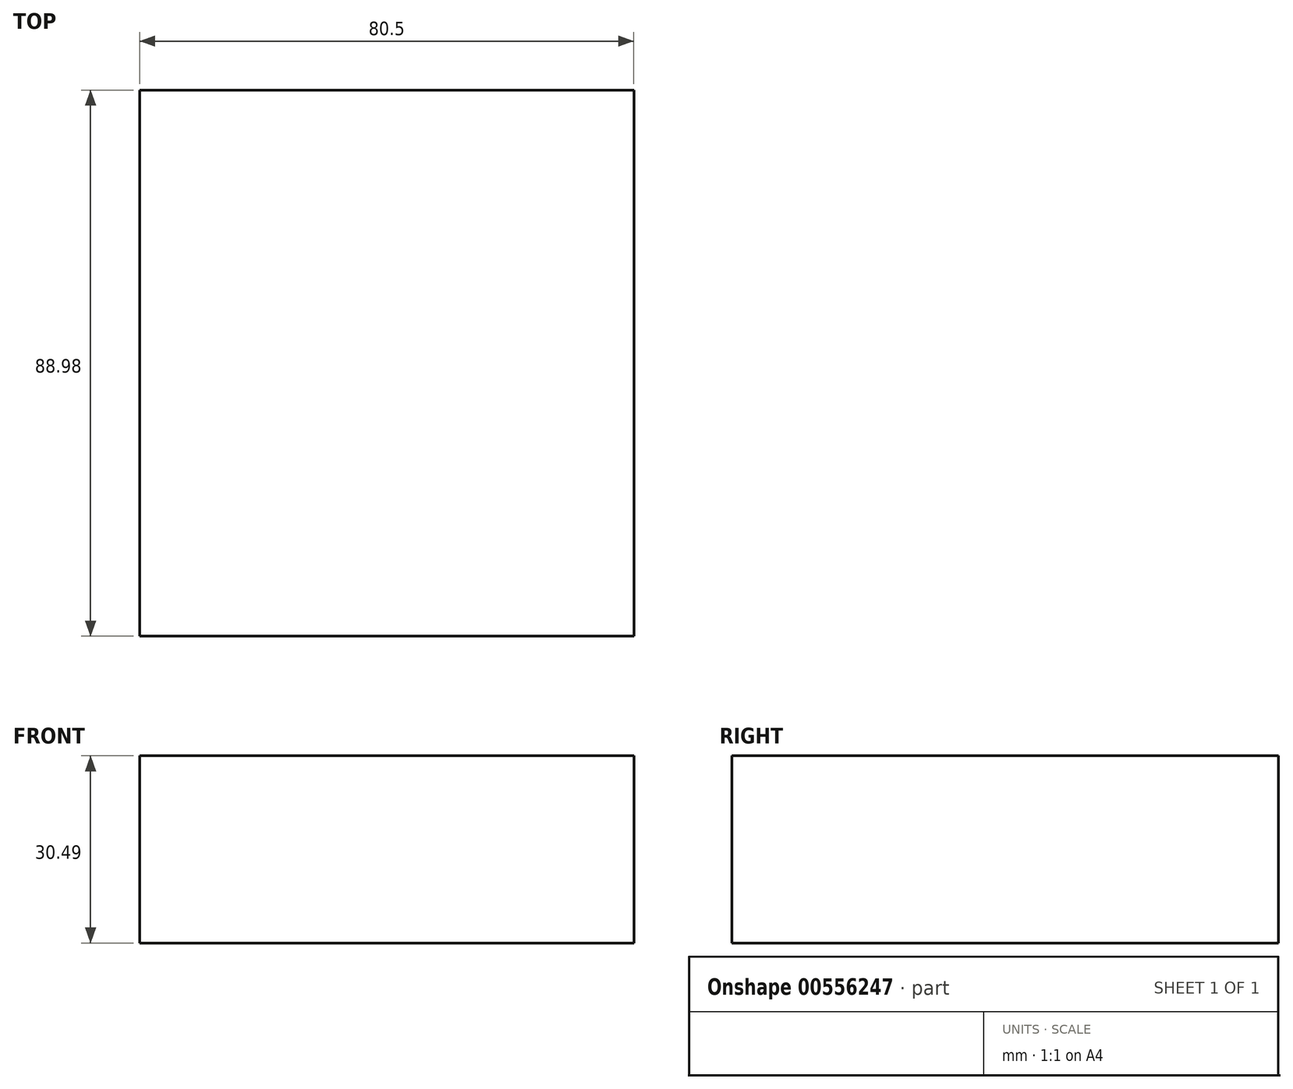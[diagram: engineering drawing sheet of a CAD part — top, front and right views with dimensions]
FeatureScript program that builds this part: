
annotation { "Feature Type Name" : "Feature", "Feature Type Description" : "" }
export const myFeature = defineFeature(function(context is Context, id is Id, definition is map)
    precondition{}
    {
        {
            var Q0;
            Q0=qCreatedBy(makeId("Top.planeOp"),FACE);
            var sketch = newSketch(context, id + "F0", { "sketchPlane" : qUnion([Q0])});
            skLineSegment(sketch, "E0.bottom", {"start": v(40.25, 44.5) * mm, "end": v(-40.25, 44.5) * mm});
            skLineSegment(sketch, "E0.top", {"start": v(40.25, -44.5) * mm, "end": v(-40.25, -44.5) * mm});
            skLineSegment(sketch, "E0.left", {"start": v(40.25, 44.5) * mm, "end": v(40.25, -44.5) * mm});
            skLineSegment(sketch, "E0.right", {"start": v(-40.25, 44.5) * mm, "end": v(-40.25, -44.5) * mm});
            skPoint(sketch, "E0.middle", {"position": v(0, 0) * mm});
            skSolve(sketch);
        }
        {
            var Q0;
            Q0=makeQuery(id+"F0.imprint","IMPRINT",FACE,{"disambiguationData":[TD([[makeQuery(id+"F0.imprint","IMPRINT",EDGE,{"derivedFrom":sQuery(id+"F0.wireOp",EDGE,"E0.bottom")}),1.0]])]});
            extrude(context, id + "F1", {"entities" : qUnion([Q0]), "depth" : 30.49 * mm, "offsetDistance" : 25.4 * mm});
        }
    });
